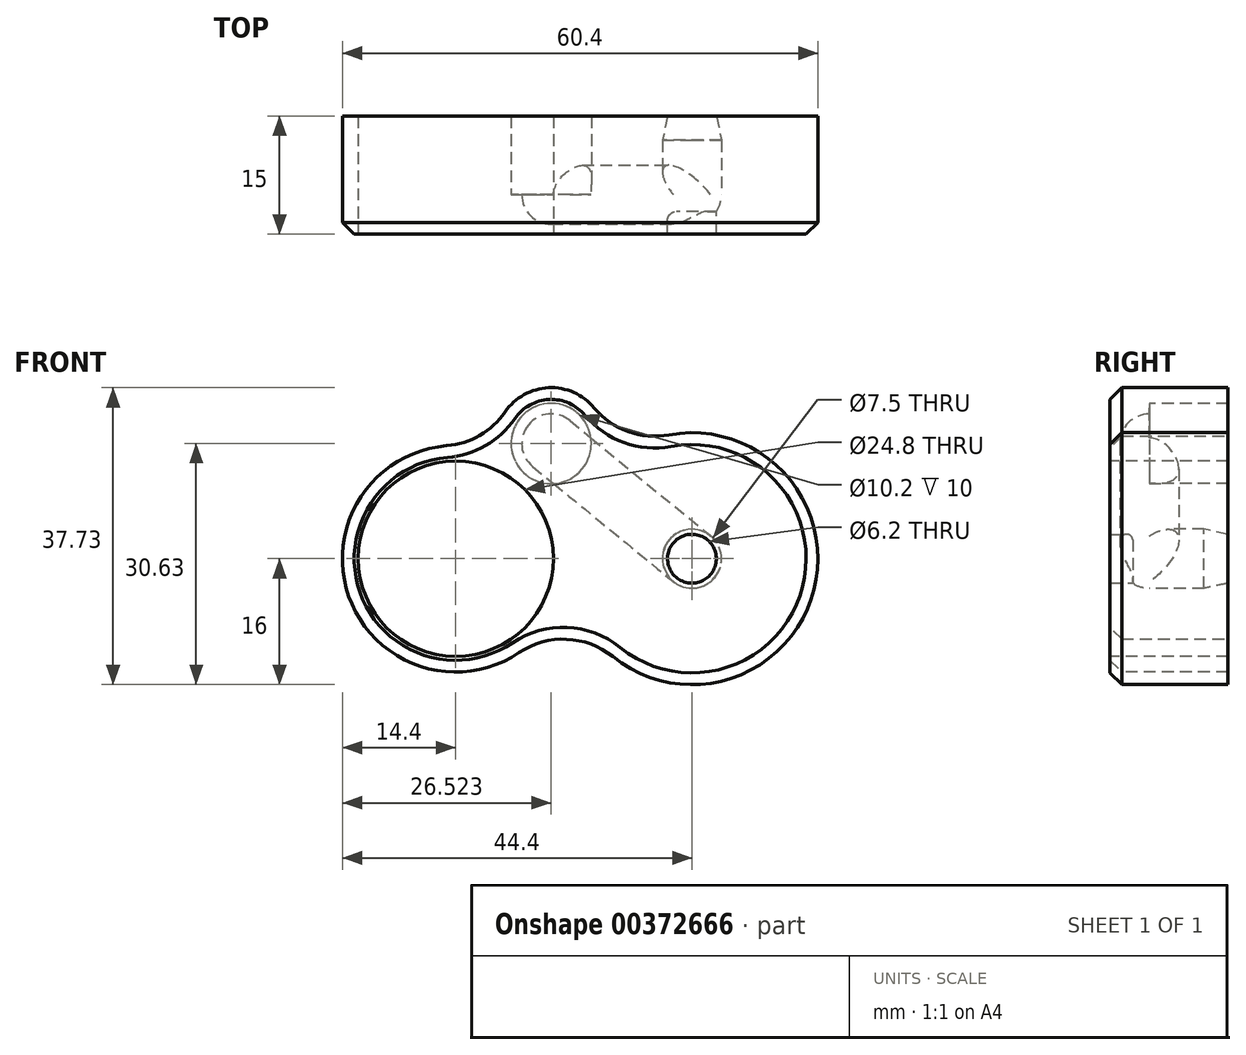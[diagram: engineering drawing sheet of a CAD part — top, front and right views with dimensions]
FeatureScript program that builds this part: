
annotation { "Feature Type Name" : "Feature", "Feature Type Description" : "" }
export const myFeature = defineFeature(function(context is Context, id is Id, definition is map)
    precondition{}
    {
        {
            var Q0;
            Q0=qCreatedBy(makeId("Front.planeOp"),FACE);
            var sketch = newSketch(context, id + "F0", { "sketchPlane" : qUnion([Q0])});
            skCircle(sketch, "E0", {"center": v(0, 0) * mm, "radius": 12.4 * mm});
            skArc(sketch, "E1", {"start": v(17.62, 10.13) * mm, "mid": v(13.95, 21.5) * mm, "end": v(5.12, 13.46) * mm});
            skArc(sketch, "E2", {"start": v(5.12, 13.46) * mm, "mid": v(-12.51, -7.13) * mm, "end": v(14.19, -2.45) * mm});
            skCircle(sketch, "E3.converted", {"center": v(12.12, 14.63) * mm, "radius": 5.1 * mm});
            skCircle(sketch, "E4", {"center": v(30, 0) * mm, "radius": 3.75 * mm});
            skArc(sketch, "E5", {"start": v(14.19, -2.45) * mm, "mid": v(45.44, -4.2) * mm, "end": v(17.62, 10.13) * mm});
            skArc(sketch, "E6", {"start": v(14.5, 17.53) * mm, "mid": v(9.22, 17) * mm, "end": v(9.75, 11.73) * mm});
            skLineSegment(sketch, "E7", {"start": v(32.37, 2.9) * mm, "end": v(14.5, 17.53) * mm});
            skLineSegment(sketch, "E8", {"start": v(9.75, 11.73) * mm, "end": v(27.63, -2.9) * mm});
            skLineSegment(sketch, "E9", {"start": v(0, 0) * mm, "end": v(12.03, 14.7) * mm, "construction": true});
            skCircle(sketch, "E10", {"center": v(0, 0) * mm, "radius": 10.9 * mm});
            skLineSegment(sketch, "E11", {"start": v(9.22, 17) * mm, "end": v(32.9, -2.37) * mm});
            skSolve(sketch);
        }
        {
            var Q0;
            Q0=makeQuery(id+"F0.imprint","IMPRINT",FACE,{"disambiguationData":[TD([[makeQuery(id+"F0.imprint","IMPRINT",EDGE,{"derivedFrom":sQuery(id+"F0.wireOp",EDGE,"E0")}),-1.0]])]});
            var Q1;
            {var subQ0=sQuery(id+"F0.wireOp",EDGE,"E5");var subQ1=sQuery(id+"F0.wireOp",EDGE,"E1");var subQ2=makeQuery(id+"F0.imprint","INTERSECT",VERTEX,{"derivedFrom":[subQ1,subQ0]});Q1=makeQuery(id+"F0.imprint","IMPRINT",FACE,{"disambiguationData":[TD([[makeQuery(id+"F0.imprint","IMPRINT",EDGE,{"disambiguationData":[TD([[subQ2,-1.0]])],"derivedFrom":subQ1}),1.0]])]});}
            var Q2;
            {var subQ3=sQuery(id+"F0.wireOp",EDGE,"E3.converted");var subQ5=sQuery(id+"F0.wireOp",EDGE,"E11");var subQ7=makeQuery(id+"F0.imprint","INTERSECT",VERTEX,{"derivedFrom":[subQ3,subQ5]});Q2=makeQuery(id+"F0.imprint","IMPRINT",FACE,{"disambiguationData":[TD([[makeQuery(id+"F0.imprint","IMPRINT",EDGE,{"disambiguationData":[TD([[subQ7,1.0]])],"derivedFrom":subQ3}),-1.0]])]});}
            var Q3;
            {var subQ0=sQuery(id+"F0.wireOp",EDGE,"E7");var subQ1=sQuery(id+"F0.wireOp",EDGE,"E4");var subQ2=makeQuery(id+"F0.imprint","INTERSECT",VERTEX,{"derivedFrom":[subQ1,subQ0]});Q3=makeQuery(id+"F0.imprint","IMPRINT",FACE,{"disambiguationData":[TD([[makeQuery(id+"F0.imprint","IMPRINT",EDGE,{"disambiguationData":[TD([[subQ2,-1.0]])],"derivedFrom":subQ1}),-1.0]])]});}
            extrude(context, id + "F1", {"entities" : qUnion([Q0, Q1, Q2, Q3]), "oppositeDirection" : true, "depth" : 10 * mm, "offsetDistance" : 25 * mm});
        }
        {
            var Q0;
            Q0=makeQuery(id+"F1.opExtrude","SWEPT_EDGE",EDGE,{"disambiguationData":[OSD([sQuery(id+"F0.wireOp",EDGE,"E1"),sQuery(id+"F0.wireOp",EDGE,"E2")])]});
            var Q1;
            Q1=makeQuery(id+"F1.opExtrude","SWEPT_EDGE",EDGE,{"disambiguationData":[OSD([sQuery(id+"F0.wireOp",EDGE,"E1"),sQuery(id+"F0.wireOp",EDGE,"E5")])]});
            var Q2;
            Q2=makeQuery(id+"F1.opExtrude","SWEPT_EDGE",EDGE,{"disambiguationData":[OSD([sQuery(id+"F0.wireOp",EDGE,"E2"),sQuery(id+"F0.wireOp",EDGE,"E5")])]});
            fillet(context, id + "F2", {"entities" : qUnion([Q0, Q1, Q2]), "radius" : 10 * mm, "tangentPropagation" : true, "allowEdgeOverflow" : false});
        }
        {
            var Q0;
            Q0=makeQuery(id+"F0.imprint","IMPRINT",FACE,{"disambiguationData":[TD([[makeQuery(id+"F0.imprint","IMPRINT",EDGE,{"derivedFrom":sQuery(id+"F0.wireOp",EDGE,"E0")}),-1.0]])]});
            var Q1;
            Q1=makeQuery(id+"F1.opExtrude","CAP_FACE",FACE,{"disambiguationData":[OSD([sQuery(id+"F0.wireOp",EDGE,"E0"),sQuery(id+"F0.wireOp",EDGE,"E1"),sQuery(id+"F0.wireOp",EDGE,"E2"),sQuery(id+"F0.wireOp",EDGE,"E3.converted"),sQuery(id+"F0.wireOp",EDGE,"E4"),sQuery(id+"F0.wireOp",EDGE,"E5"),sQuery(id+"F0.wireOp",EDGE,"E7")])],"isStart":true});
            var Q2;
            {var subQ0=sQuery(id+"F0.wireOp",EDGE,"E5");var subQ1=sQuery(id+"F0.wireOp",EDGE,"E1");var subQ2=makeQuery(id+"F0.imprint","INTERSECT",VERTEX,{"derivedFrom":[subQ1,subQ0]});Q2=makeQuery(id+"F0.imprint","IMPRINT",FACE,{"disambiguationData":[TD([[makeQuery(id+"F0.imprint","IMPRINT",EDGE,{"disambiguationData":[TD([[subQ2,-1.0]])],"derivedFrom":subQ1}),1.0]])]});}
            var Q3;
            {var subQ5=sQuery(id+"F0.wireOp",EDGE,"E6");Q3=makeQuery(id+"F0.imprint","IMPRINT",FACE,{"disambiguationData":[TD([[makeQuery(id+"F0.imprint","IMPRINT",EDGE,{"derivedFrom":subQ5}),1.0]])]});}
            var Q4;
            {var subQ5=sQuery(id+"F0.wireOp",EDGE,"E6");Q4=makeQuery(id+"F0.imprint","IMPRINT",FACE,{"disambiguationData":[TD([[makeQuery(id+"F0.imprint","IMPRINT",EDGE,{"derivedFrom":subQ5}),-1.0]])]});}
            var Q5;
            {var subQ0=sQuery(id+"F0.wireOp",EDGE,"E4");var subQ1=makeQuery(id+"F0.imprint","INTERSECT",VERTEX,{"derivedFrom":[subQ0,sQuery(id+"F0.wireOp",EDGE,"E7")]});Q5=makeQuery(id+"F0.imprint","IMPRINT",FACE,{"disambiguationData":[TD([[makeQuery(id+"F0.imprint","IMPRINT",EDGE,{"disambiguationData":[TD([[subQ1,-1.0]])],"derivedFrom":subQ0}),1.0]])]});}
            var Q6;
            {var subQ0=sQuery(id+"F0.wireOp",EDGE,"E4");var subQ1=makeQuery(id+"F0.imprint","INTERSECT",VERTEX,{"derivedFrom":[subQ0,sQuery(id+"F0.wireOp",EDGE,"E8")]});Q6=makeQuery(id+"F0.imprint","IMPRINT",FACE,{"disambiguationData":[TD([[makeQuery(id+"F0.imprint","IMPRINT",EDGE,{"disambiguationData":[TD([[subQ1,1.0]])],"derivedFrom":subQ0}),1.0]])]});}
            extrude(context, id + "F3", {"entities" : qUnion([Q0, Q1, Q2, Q3, Q4, Q5, Q6]), "operationType" : NewBodyOperationType.ADD, "depth" : 5 * mm, "offsetDistance" : 25 * mm});
        }
        {
            var Q0;
            {var subQ5=sQuery(id+"F0.wireOp",EDGE,"E6");Q0=makeQuery(id+"F0.imprint","IMPRINT",FACE,{"disambiguationData":[TD([[makeQuery(id+"F0.imprint","IMPRINT",EDGE,{"derivedFrom":subQ5}),-1.0]])]});}
            extrude(context, id + "F4", {"entities" : qUnion([Q0]), "operationType" : NewBodyOperationType.ADD, "depth" : 3 * mm, "offsetDistance" : 25 * mm});
        }
        {
            var Q0;
            {var subQ0=sQuery(id+"F0.wireOp",EDGE,"E11");var subQ1=sQuery(id+"F0.wireOp",EDGE,"E3.converted");var subQ2=makeQuery(id+"F0.imprint","INTERSECT",VERTEX,{"derivedFrom":[subQ1,subQ0]});Q0=makeQuery(id+"F0.imprint","IMPRINT",FACE,{"disambiguationData":[TD([[makeQuery(id+"F0.imprint","IMPRINT",EDGE,{"disambiguationData":[TD([[subQ2,-1.0]])],"derivedFrom":subQ1}),1.0]])]});}
            var Q1;
            {var subQ0=sQuery(id+"F0.wireOp",EDGE,"E11");var subQ5=sQuery(id+"F0.wireOp",EDGE,"E3.converted");var subQ6=makeQuery(id+"F0.imprint","INTERSECT",VERTEX,{"derivedFrom":[subQ5,subQ0]});Q1=makeQuery(id+"F0.imprint","IMPRINT",FACE,{"disambiguationData":[TD([[makeQuery(id+"F0.imprint","IMPRINT",EDGE,{"disambiguationData":[TD([[subQ6,-1.0]])],"derivedFrom":subQ5}),-1.0]])]});}
            var Q2;
            {var subQ0=sQuery(id+"F0.wireOp",EDGE,"E7");var subQ1=sQuery(id+"F0.wireOp",EDGE,"E4");var subQ2=makeQuery(id+"F0.imprint","INTERSECT",VERTEX,{"derivedFrom":[subQ1,subQ0]});Q2=makeQuery(id+"F0.imprint","IMPRINT",FACE,{"disambiguationData":[TD([[makeQuery(id+"F0.imprint","IMPRINT",EDGE,{"disambiguationData":[TD([[subQ2,-1.0]])],"derivedFrom":subQ1}),-1.0]])]});}
            var Q3;
            {var subQ0=sQuery(id+"F0.wireOp",EDGE,"E4");var subQ1=makeQuery(id+"F0.imprint","INTERSECT",VERTEX,{"derivedFrom":[subQ0,sQuery(id+"F0.wireOp",EDGE,"E7")]});Q3=makeQuery(id+"F0.imprint","IMPRINT",FACE,{"disambiguationData":[TD([[makeQuery(id+"F0.imprint","IMPRINT",EDGE,{"disambiguationData":[TD([[subQ1,-1.0]])],"derivedFrom":subQ0}),1.0]])]});}
            var Q4;
            {var subQ1=sQuery(id+"F0.wireOp",EDGE,"E1");var subQ3=sQuery(id+"F0.wireOp",EDGE,"E7");var subQ4=makeQuery(id+"F0.imprint","INTERSECT",VERTEX,{"derivedFrom":[subQ1,subQ3]});Q4=makeQuery(id+"F0.imprint","IMPRINT",FACE,{"disambiguationData":[TD([[makeQuery(id+"F0.imprint","IMPRINT",EDGE,{"disambiguationData":[TD([[subQ4,1.0]])],"derivedFrom":subQ3}),1.0]])]});}
            var Q5;
            Q5=sQuery(id+"F0.wireOp",EDGE,"E11");
            revolve(context, id + "F5", {"operationType" : NewBodyOperationType.REMOVE, "surfaceOperationType" : NewSurfaceOperationType.NEW, "entities" : qUnion([Q0, Q1, Q2, Q3, Q4]), "axis" : qUnion([Q5]), "revolveType" : RevolveType.FULL, "oppositeDirection" : true});
        }
        {
            var Q0;
            {var subQ0=sQuery(id+"F0.wireOp",EDGE,"E5");Q0=makeQuery(id+"F3.opExtrude","CAP_EDGE",EDGE,{"disambiguationData":[OSD([subQ0]),TDD([makeQuery(id+"F0.imprint","IMPRINT",EDGE,{"disambiguationData":[TD([[makeQuery(id+"F0.imprint","INTERSECT",VERTEX,{"derivedFrom":[sQuery(id+"F0.wireOp",EDGE,"E2"),subQ0]}),-1.0]])],"derivedFrom":subQ0}),makeQuery(id+"F0.imprint","IMPRINT",EDGE,{"disambiguationData":[TD([[makeQuery(id+"F0.imprint","INTERSECT",VERTEX,{"derivedFrom":[sQuery(id+"F0.wireOp",EDGE,"E1"),subQ0]}),1.0]])],"derivedFrom":subQ0})])],"isStart":false});}
            var Q1;
            {var subQ0=sQuery(id+"F0.wireOp",EDGE,"E7");var subQ1=sQuery(id+"F0.wireOp",EDGE,"E5");var subQ2=sQuery(id+"F0.wireOp",EDGE,"E4");var subQ3=sQuery(id+"F0.wireOp",EDGE,"E3.converted");var subQ4=sQuery(id+"F0.wireOp",EDGE,"E2");var subQ5=sQuery(id+"F0.wireOp",EDGE,"E1");var subQ6=sQuery(id+"F0.wireOp",EDGE,"E0");Q1=makeQuery(id+"F3.opExtrude","CAP_EDGE",EDGE,{"disambiguationData":[OSD([subQ6,subQ5,subQ4,subQ3,subQ2,subQ1,subQ0]),TDD([makeQuery(id+"F2.opFillet","BLEND_EDGE",EDGE,{"blendedFrom":[makeQuery(id+"F1.opExtrude","SWEPT_EDGE",EDGE,{"disambiguationData":[OSD([subQ4,subQ1])]}),makeQuery(id+"F1.opExtrude","CAP_FACE",FACE,{"disambiguationData":[OSD([subQ6,subQ5,subQ4,subQ3,subQ2,subQ1,subQ0])],"isStart":true})],"blendedInto":[makeQuery(id+"F1.opExtrude","CAP_FACE",FACE,{"disambiguationData":[OSD([subQ6,subQ5,subQ4,subQ3,subQ2,subQ1,subQ0])],"isStart":true})]})])],"isStart":false});}
            var Q2;
            {var subQ0=sQuery(id+"F0.wireOp",EDGE,"E2");Q2=makeQuery(id+"F3.opExtrude","CAP_EDGE",EDGE,{"disambiguationData":[OSD([subQ0]),TDD([makeQuery(id+"F0.imprint","IMPRINT",EDGE,{"derivedFrom":subQ0})])],"isStart":false});}
            var Q3;
            {var subQ0=sQuery(id+"F0.wireOp",EDGE,"E7");var subQ1=sQuery(id+"F0.wireOp",EDGE,"E5");var subQ2=sQuery(id+"F0.wireOp",EDGE,"E4");var subQ3=sQuery(id+"F0.wireOp",EDGE,"E3.converted");var subQ4=sQuery(id+"F0.wireOp",EDGE,"E2");var subQ5=sQuery(id+"F0.wireOp",EDGE,"E1");var subQ6=sQuery(id+"F0.wireOp",EDGE,"E0");Q3=makeQuery(id+"F3.opExtrude","CAP_EDGE",EDGE,{"disambiguationData":[OSD([subQ6,subQ5,subQ4,subQ3,subQ2,subQ1,subQ0]),TDD([makeQuery(id+"F2.opFillet","BLEND_EDGE",EDGE,{"blendedFrom":[makeQuery(id+"F1.opExtrude","SWEPT_EDGE",EDGE,{"disambiguationData":[OSD([subQ5,subQ4])]}),makeQuery(id+"F1.opExtrude","CAP_FACE",FACE,{"disambiguationData":[OSD([subQ6,subQ5,subQ4,subQ3,subQ2,subQ1,subQ0])],"isStart":true})],"blendedInto":[makeQuery(id+"F1.opExtrude","CAP_FACE",FACE,{"disambiguationData":[OSD([subQ6,subQ5,subQ4,subQ3,subQ2,subQ1,subQ0])],"isStart":true})]})])],"isStart":false});}
            var Q4;
            {var subQ0=sQuery(id+"F0.wireOp",EDGE,"E1");Q4=makeQuery(id+"F3.opExtrude","CAP_EDGE",EDGE,{"disambiguationData":[OSD([subQ0]),TDD([makeQuery(id+"F0.imprint","IMPRINT",EDGE,{"disambiguationData":[TD([[makeQuery(id+"F0.imprint","INTERSECT",VERTEX,{"derivedFrom":[subQ0,sQuery(id+"F0.wireOp",EDGE,"E5")]}),-1.0]])],"derivedFrom":subQ0}),makeQuery(id+"F0.imprint","IMPRINT",EDGE,{"disambiguationData":[TD([[makeQuery(id+"F0.imprint","INTERSECT",VERTEX,{"derivedFrom":[subQ0,sQuery(id+"F0.wireOp",EDGE,"E2")]}),1.0]])],"derivedFrom":subQ0})])],"isStart":false});}
            var Q5;
            {var subQ0=sQuery(id+"F0.wireOp",EDGE,"E7");var subQ1=sQuery(id+"F0.wireOp",EDGE,"E5");var subQ2=sQuery(id+"F0.wireOp",EDGE,"E4");var subQ3=sQuery(id+"F0.wireOp",EDGE,"E3.converted");var subQ4=sQuery(id+"F0.wireOp",EDGE,"E2");var subQ5=sQuery(id+"F0.wireOp",EDGE,"E1");var subQ6=sQuery(id+"F0.wireOp",EDGE,"E0");Q5=makeQuery(id+"F3.opExtrude","CAP_EDGE",EDGE,{"disambiguationData":[OSD([subQ6,subQ5,subQ4,subQ3,subQ2,subQ1,subQ0]),TDD([makeQuery(id+"F2.opFillet","BLEND_EDGE",EDGE,{"blendedFrom":[makeQuery(id+"F1.opExtrude","SWEPT_EDGE",EDGE,{"disambiguationData":[OSD([subQ1,subQ0])]}),makeQuery(id+"F1.opExtrude","CAP_FACE",FACE,{"disambiguationData":[OSD([subQ6,subQ5,subQ4,subQ3,subQ2,subQ1,subQ0])],"isStart":true})],"blendedInto":[makeQuery(id+"F1.opExtrude","CAP_FACE",FACE,{"disambiguationData":[OSD([subQ6,subQ5,subQ4,subQ3,subQ2,subQ1,subQ0])],"isStart":true})]})])],"isStart":false});}
            var Q6;
            {var subQ0=sQuery(id+"F0.wireOp",EDGE,"E7");var subQ1=sQuery(id+"F0.wireOp",EDGE,"E5");var subQ2=sQuery(id+"F0.wireOp",EDGE,"E4");var subQ3=sQuery(id+"F0.wireOp",EDGE,"E3.converted");var subQ4=sQuery(id+"F0.wireOp",EDGE,"E2");var subQ5=sQuery(id+"F0.wireOp",EDGE,"E1");var subQ6=sQuery(id+"F0.wireOp",EDGE,"E0");Q6=makeQuery(id+"F3.opExtrude","CAP_EDGE",EDGE,{"disambiguationData":[OSD([subQ6,subQ5,subQ4,subQ3,subQ2,subQ1,subQ0]),TDD([makeQuery(id+"F2.opFillet","BLEND_EDGE",EDGE,{"blendedFrom":[makeQuery(id+"F1.opExtrude","SWEPT_EDGE",EDGE,{"disambiguationData":[OSD([subQ5,subQ0])]}),makeQuery(id+"F1.opExtrude","CAP_FACE",FACE,{"disambiguationData":[OSD([subQ6,subQ5,subQ4,subQ3,subQ2,subQ1,subQ0])],"isStart":true})],"blendedInto":[makeQuery(id+"F1.opExtrude","CAP_FACE",FACE,{"disambiguationData":[OSD([subQ6,subQ5,subQ4,subQ3,subQ2,subQ1,subQ0])],"isStart":true})]})])],"isStart":false});}
            chamfer(context, id + "F6", {"entities" : qUnion([Q0, Q1, Q2, Q3, Q4, Q5, Q6]), "width" : 1.5 * mm, "tangentPropagation" : true});
        }
        {
            var Q0;
            Q0=makeQuery(id+"F1.opExtrude","CAP_FACE",FACE,{"disambiguationData":[OSD([sQuery(id+"F0.wireOp",EDGE,"E0"),sQuery(id+"F0.wireOp",EDGE,"E1"),sQuery(id+"F0.wireOp",EDGE,"E2"),sQuery(id+"F0.wireOp",EDGE,"E3.converted"),sQuery(id+"F0.wireOp",EDGE,"E4"),sQuery(id+"F0.wireOp",EDGE,"E5")])],"isStart":false});
            var sketch = newSketch(context, id + "F7", { "sketchPlane" : qUnion([Q0])});
            skCircle(sketch, "E12.0", {"center": v(-30, 0) * mm, "radius": 5 * mm});
            skCircle(sketch, "E13", {"center": v(-30, 0) * mm, "radius": 3.1 * mm});
            skSolve(sketch);
        }
        {
            var Q0;
            Q0=makeQuery(id+"F7.imprint","IMPRINT",FACE,{"disambiguationData":[TD([[makeQuery(id+"F7.imprint","IMPRINT",EDGE,{"derivedFrom":sQuery(id+"F7.wireOp",EDGE,"E12.0")}),1.0]])]});
            var Q1;
            Q1=makeQuery(id+"F7.imprint","IMPRINT",FACE,{"disambiguationData":[TD([[makeQuery(id+"F7.imprint","IMPRINT",EDGE,{"derivedFrom":sQuery(id+"F7.wireOp",EDGE,"E13")}),-1.0]])]});
            extrude(context, id + "F8", {"entities" : qUnion([Q0, Q1]), "operationType" : NewBodyOperationType.ADD, "oppositeDirection" : true, "depth" : 5 * mm, "offsetDistance" : 25 * mm, "hasDraft" : true, "draftAngle" : 12 * degree, "draftPullDirection" : true});
        }
        {
            var Q0;
            Q0=makeQuery(id+"F7.imprint","IMPRINT",FACE,{"disambiguationData":[TD([[makeQuery(id+"F7.imprint","IMPRINT",EDGE,{"derivedFrom":sQuery(id+"F7.wireOp",EDGE,"E13")}),1.0]])]});
            extrude(context, id + "F9", {"entities" : qUnion([Q0]), "operationType" : NewBodyOperationType.REMOVE, "endBound" : BoundingType.THROUGH_ALL, "oppositeDirection" : true, "depth" : 25 * mm, "offsetDistance" : 25 * mm});
        }
    });
